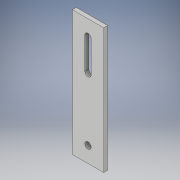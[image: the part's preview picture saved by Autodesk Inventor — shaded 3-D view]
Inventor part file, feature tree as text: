
AUTODESK INVENTOR PART (.ipt)
format: ipt  version: 2018 (Build 220112000, 112)  size: 104,448 bytes
history: native  units: in
note: dims shown in document units (in); Inventor stores cm internally (conversion verified against a paired STEP export)
features: extrude x1, sketch x1
ambient origin geometry x8: Origin, YZ Plane, XZ Plane, XY Plane, X Axis, Y Axis, Z Axis, Center Point
bodies: Body1 (feature_tree)
feature tree (2):
  extrude  "Extrusion2"  Depth=4.0in
  sketch  "Sketch1"  dims[d0=1.0in d1=4.0in d2=0.5in d3=0.5in d7=1.0in d8=0.125in d9=0.0in]
